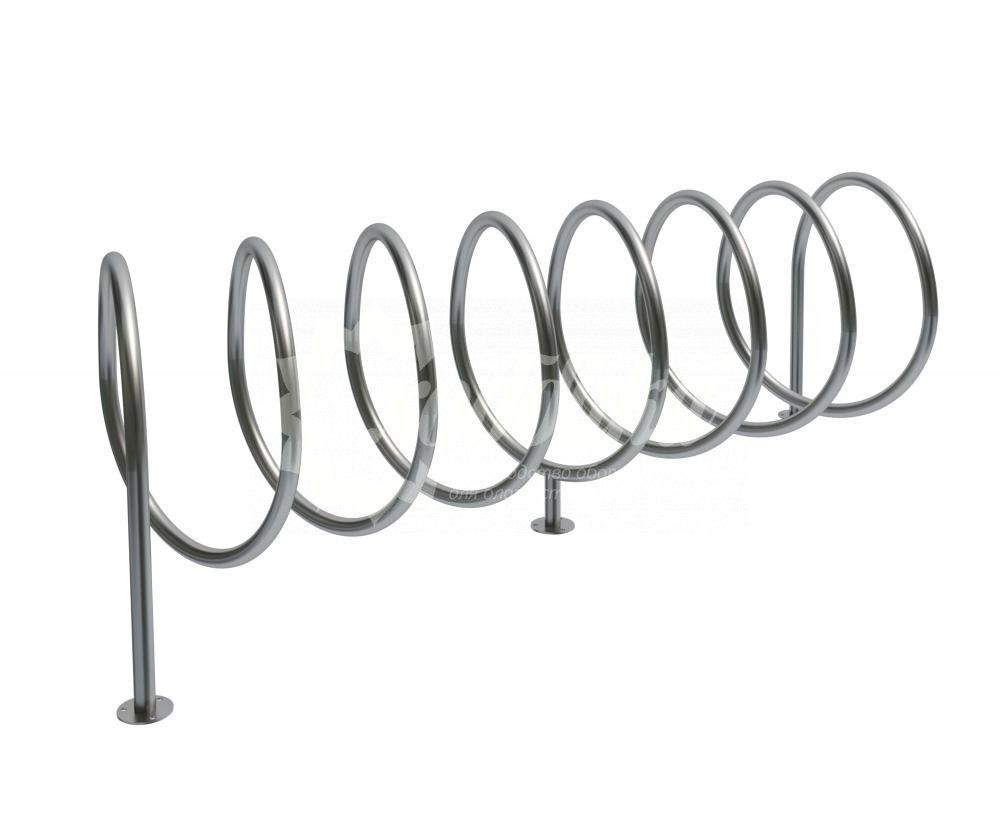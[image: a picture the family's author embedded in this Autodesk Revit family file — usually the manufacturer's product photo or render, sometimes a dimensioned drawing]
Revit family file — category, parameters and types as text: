
# Revit family: Велопарковка из нержавеющей стали «Спираль» Арт 10668 — копия
name_source: partatom
category: Антураж
revit_build: Autodesk Revit 2018 (Build: 20180423_1000(x64)
units: mm (PartAtom-declared; Revit-internal decimal feet)

## family parameters
Всегда вертикально = Да
Источник визуального образа = Геометрия семейства
На основе рабочей плоскости = Нет
Общий = Нет
При загрузке вырезать с полостями = Нет
Точка расчета площади = Нет

## types (4) — shared parameters
Артикул товара = Арт. 10668
Высота = 650 мм
Группа модели = Велопарковки для велосипедов
Изготовитель = ООО «Хоббика»
Изображение типоразмера = Велопарковка спираль.jpg
Материал изделия = Нержавеющая сталь
Цвет каркаса = Хромированая сталь
Ширина = 550 мм

## per-type parameters (varying)
| type | URL | Длина | Модель на 10 мест | Модель на 12 мест | Модель на 5 мест | Модель на 7 мест | Описание |
| Модель на 7 мест |  | 1910 мм | Нет | Нет | Нет | Да | Велопарковка из нержавеющей стали «Спираль» Модель на 7 мест |
| Модель на 5 мест |  | 1410 мм | Нет | Нет | Да | Нет | Велопарковка из нержавеющей стали «Спираль» Модель на 5 мест |
| Модель на 10 мест | https://hobbyka.ru | 2660 мм | Да | Нет | Нет | Нет | Велопарковка из нержавеющей стали «Спираль» Модель на 10 мест |
| Модель на 12 мест |  | 3160 мм | Нет | Да | Нет | Нет | Велопарковка из нержавеющей стали «Спираль» Модель на 12 мест |
